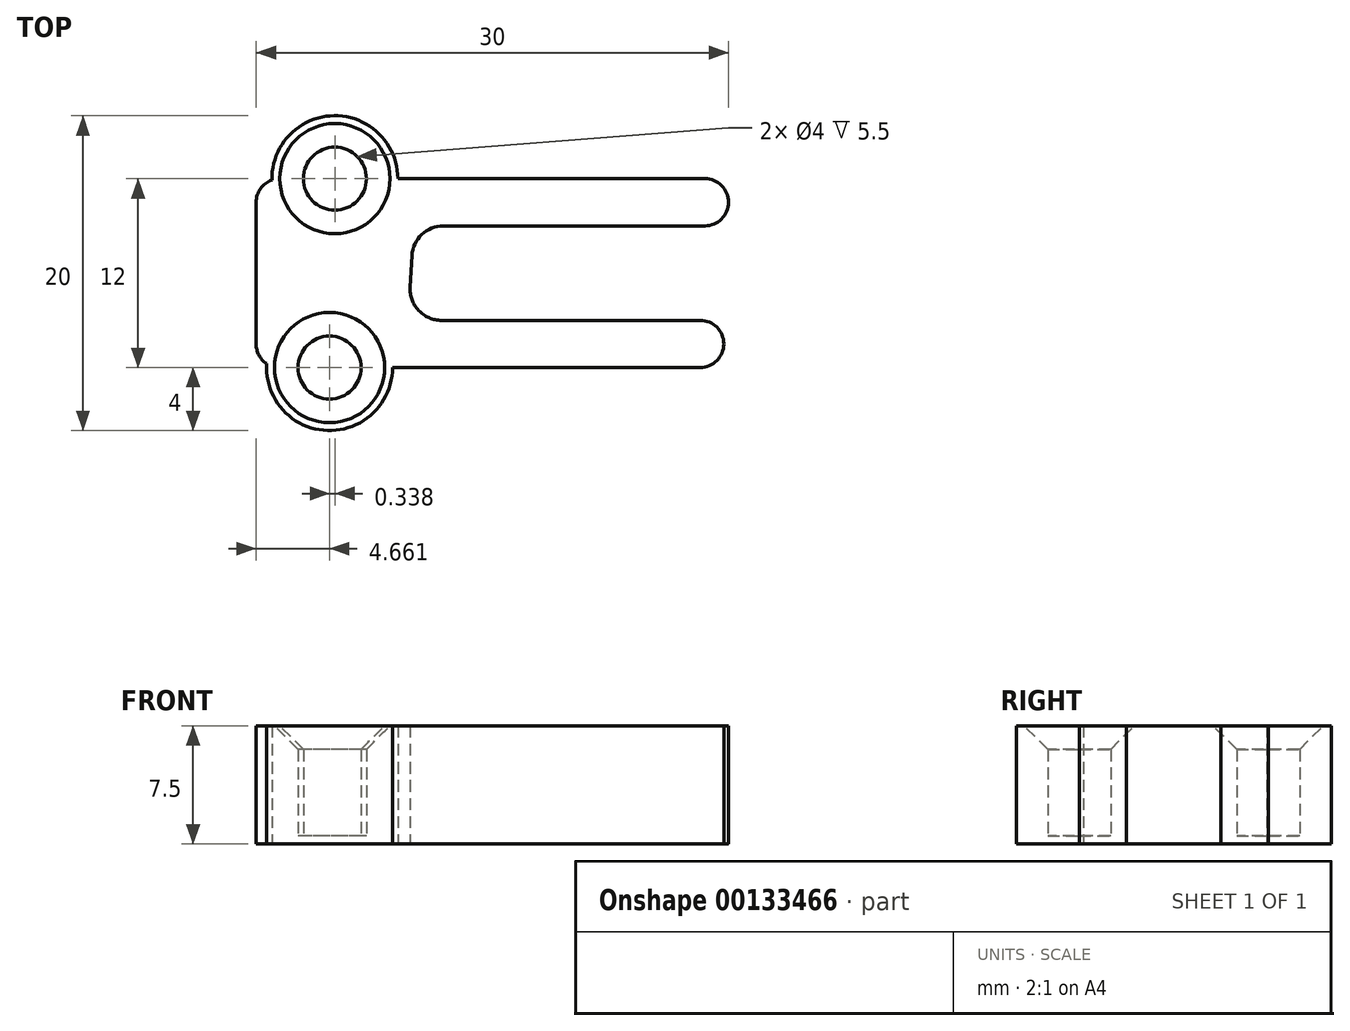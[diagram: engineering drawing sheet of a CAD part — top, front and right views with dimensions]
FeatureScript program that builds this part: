
annotation { "Feature Type Name" : "Feature", "Feature Type Description" : "" }
export const myFeature = defineFeature(function(context is Context, id is Id, definition is map)
    precondition{}
    {
        {
            var Q0;
            Q0=qCreatedBy(makeId("Top.planeOp"),FACE);
            var sketch = newSketch(context, id + "F0", { "sketchPlane" : qUnion([Q0])});
            skLineSegment(sketch, "E0.bottom", {"start": v(8.37, -3) * mm, "end": v(-8.05, -3) * mm});
            skLineSegment(sketch, "E0.top", {"start": v(8.67, 3) * mm, "end": v(-7.94, 3) * mm});
            skLineSegment(sketch, "E0.right", {"start": v(-10.05, -0.89) * mm, "end": v(-9.94, 1.11) * mm});
            skPoint(sketch, "E0.middle", {"position": v(0, 0) * mm});
            skLineSegment(sketch, "E1", {"start": v(10.17, 4.5) * mm, "end": v(10.17, 4.5) * mm});
            skLineSegment(sketch, "E2", {"start": v(8.67, 6) * mm, "end": v(-18.33, 6) * mm});
            skLineSegment(sketch, "E3", {"start": v(-19.83, 4.5) * mm, "end": v(-19.83, -4.5) * mm});
            skLineSegment(sketch, "E4", {"start": v(-18.33, -6) * mm, "end": v(8.37, -6) * mm});
            skLineSegment(sketch, "E5", {"start": v(9.87, -4.46) * mm, "end": v(9.87, -4.46) * mm});
            skPoint(sketch, "E6.visualSharp", {"position": v(-9.83, 3) * mm});
            skArc(sketch, "E6.filletArc", {"start": v(-7.94, 3) * mm, "mid": v(-9.31, 2.45) * mm, "end": v(-9.94, 1.11) * mm});
            skPoint(sketch, "E7.visualSharp", {"position": v(-10.17, -3) * mm});
            skArc(sketch, "E7.filletArc", {"start": v(-10.05, -0.89) * mm, "mid": v(-9.5, -2.37) * mm, "end": v(-8.05, -3) * mm});
            skPoint(sketch, "E8.visualSharp", {"position": v(10.17, 3) * mm});
            skArc(sketch, "E8.filletArc", {"start": v(8.67, 3) * mm, "mid": v(9.73, 3.44) * mm, "end": v(10.17, 4.5) * mm});
            skPoint(sketch, "E9.visualSharp", {"position": v(10.17, 6) * mm});
            skArc(sketch, "E9.filletArc", {"start": v(10.17, 4.5) * mm, "mid": v(9.73, 5.56) * mm, "end": v(8.67, 6) * mm});
            skPoint(sketch, "E10.visualSharp", {"position": v(-19.83, 6) * mm});
            skArc(sketch, "E10.filletArc", {"start": v(-18.33, 6) * mm, "mid": v(-19.4, 5.56) * mm, "end": v(-19.83, 4.5) * mm});
            skPoint(sketch, "E11.visualSharp", {"position": v(-19.83, -6) * mm});
            skArc(sketch, "E11.filletArc", {"start": v(-19.83, -4.5) * mm, "mid": v(-19.4, -5.56) * mm, "end": v(-18.33, -6) * mm});
            skPoint(sketch, "E12.visualSharp", {"position": v(9.83, -3) * mm});
            skArc(sketch, "E12.filletArc", {"start": v(9.87, -4.46) * mm, "mid": v(9.42, -3.43) * mm, "end": v(8.37, -3) * mm});
            skPoint(sketch, "E13", {"position": v(-10.17, -6) * mm});
            skPoint(sketch, "E14", {"position": v(-9.83, 6) * mm});
            skCircle(sketch, "E15", {"center": v(-14.83, 6) * mm, "radius": 4 * mm});
            skCircle(sketch, "E16", {"center": v(-15.17, -6) * mm, "radius": 4 * mm});
            skCircle(sketch, "E17", {"center": v(-14.83, 6) * mm, "radius": 2 * mm});
            skCircle(sketch, "E18", {"center": v(-15.17, -6) * mm, "radius": 2 * mm});
            skPoint(sketch, "E19.visualSharp", {"position": v(9.9, -6) * mm});
            skArc(sketch, "E19.filletArc", {"start": v(8.37, -6) * mm, "mid": v(9.44, -5.55) * mm, "end": v(9.87, -4.46) * mm});
            skSolve(sketch);
        }
        {
            var Q0;
            Q0 = qSketchRegion(id + "F0", true);
            extrude(context, id + "F1", {"entities" : qUnion([Q0]), "depth" : 7 * mm});
        }
        {
            var Q0;
            Q0 = qSketchRegion(id + "F0", true);
            var Q1;
            {var subQ0=sQuery(id+"F0.wireOp",EDGE,"E17");var subQ1=sQuery(id+"F0.wireOp",EDGE,"E2");var subQ2=makeQuery(id+"F0.imprint","INTERSECT",VERTEX,{"disambiguationData":[OD(0.0)],"derivedFrom":[subQ1,subQ0]});Q1=makeQuery(id+"F0.imprint","IMPRINT",FACE,{"disambiguationData":[TD([[makeQuery(id+"F0.imprint","IMPRINT",EDGE,{"disambiguationData":[TD([[subQ2,-1.0]])],"derivedFrom":subQ1}),-1.0]])]});}
            var Q2;
            {var subQ0=sQuery(id+"F0.wireOp",EDGE,"E17");var subQ1=sQuery(id+"F0.wireOp",EDGE,"E2");var subQ2=makeQuery(id+"F0.imprint","INTERSECT",VERTEX,{"disambiguationData":[OD(0.0)],"derivedFrom":[subQ1,subQ0]});Q2=makeQuery(id+"F0.imprint","IMPRINT",FACE,{"disambiguationData":[TD([[makeQuery(id+"F0.imprint","IMPRINT",EDGE,{"disambiguationData":[TD([[subQ2,-1.0]])],"derivedFrom":subQ1}),1.0]])]});}
            var Q3;
            {var subQ0=sQuery(id+"F0.wireOp",EDGE,"E18");var subQ1=sQuery(id+"F0.wireOp",EDGE,"E4");var subQ2=makeQuery(id+"F0.imprint","INTERSECT",VERTEX,{"disambiguationData":[OD(0.0)],"derivedFrom":[subQ1,subQ0]});Q3=makeQuery(id+"F0.imprint","IMPRINT",FACE,{"disambiguationData":[TD([[makeQuery(id+"F0.imprint","IMPRINT",EDGE,{"disambiguationData":[TD([[subQ2,-1.0]])],"derivedFrom":subQ1}),1.0]])]});}
            var Q4;
            {var subQ0=sQuery(id+"F0.wireOp",EDGE,"E18");var subQ1=sQuery(id+"F0.wireOp",EDGE,"E4");var subQ2=makeQuery(id+"F0.imprint","INTERSECT",VERTEX,{"disambiguationData":[OD(0.0)],"derivedFrom":[subQ1,subQ0]});Q4=makeQuery(id+"F0.imprint","IMPRINT",FACE,{"disambiguationData":[TD([[makeQuery(id+"F0.imprint","IMPRINT",EDGE,{"disambiguationData":[TD([[subQ2,-1.0]])],"derivedFrom":subQ1}),-1.0]])]});}
            extrude(context, id + "F2", {"entities" : qUnion([Q0, Q1, Q2, Q3, Q4]), "operationType" : NewBodyOperationType.ADD, "oppositeDirection" : true, "depth" : .5 * mm});
        }
        {
            var Q0;
            Q0=makeQuery(id+"F1.opExtrude","CAP_EDGE",EDGE,{"disambiguationData":[OSD([sQuery(id+"F0.wireOp",EDGE,"E17")])],"isStart":false});
            var Q1;
            Q1=makeQuery(id+"F1.opExtrude","CAP_EDGE",EDGE,{"disambiguationData":[OSD([sQuery(id+"F0.wireOp",EDGE,"E18")])],"isStart":false});
            chamfer(context, id + "F3", {"entities" : qUnion([Q0, Q1]), "width" : 1.5 * mm, "tangentPropagation" : true});
        }
    });
